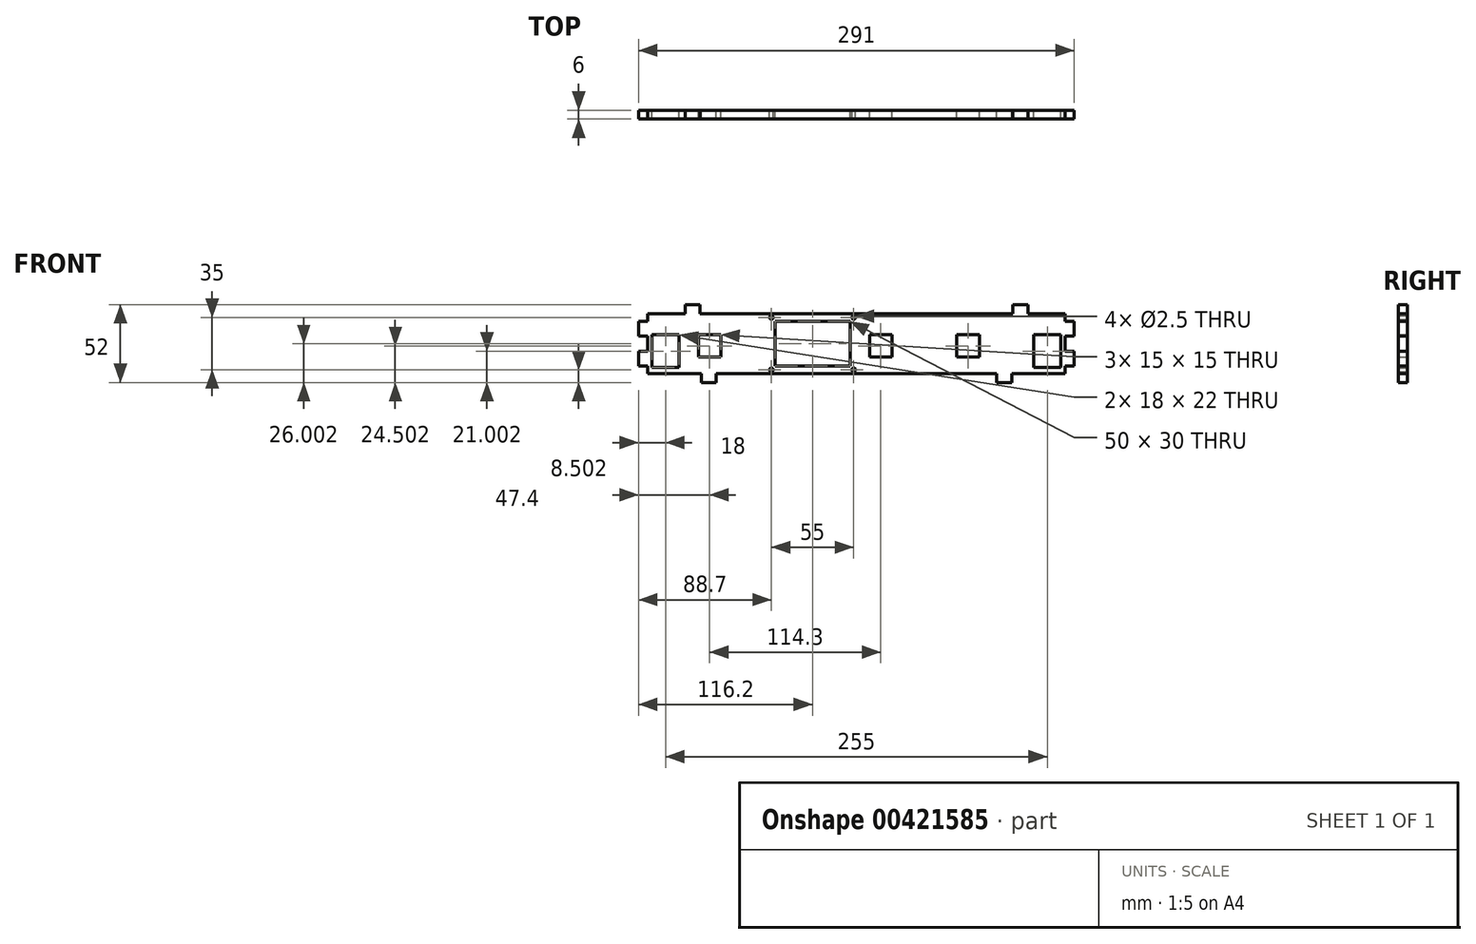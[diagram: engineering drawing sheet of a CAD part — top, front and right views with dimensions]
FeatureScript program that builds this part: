
annotation { "Feature Type Name" : "Feature", "Feature Type Description" : "" }
export const myFeature = defineFeature(function(context is Context, id is Id, definition is map)
    precondition{}
    {
        {
            var Q0;
            Q0=qCreatedBy(makeId("Front.planeOp"),FACE);
            var sketch = newSketch(context, id + "F0", { "sketchPlane" : qUnion([Q0])});
            skLineSegment(sketch, "E0", {"start": v(-139.5, -18.73) * mm, "end": v(-103.67, -18.73) * mm});
            skLineSegment(sketch, "E1.MirrorCS", {"start": v(-139.5, 21.27) * mm, "end": v(-114.5, 21.27) * mm});
            skLineSegment(sketch, "E2.MirrorCS", {"start": v(-114.5, 27.27) * mm, "end": v(-104.5, 27.27) * mm});
            skLineSegment(sketch, "E3.MirrorCS", {"start": v(-139.5, 16.27) * mm, "end": v(-139.5, 21.27) * mm});
            skLineSegment(sketch, "E4.MirrorCS", {"start": v(-139.5, 6.27) * mm, "end": v(-145.5, 6.27) * mm});
            skLineSegment(sketch, "E5.MirrorCS", {"start": v(-139.5, -3.73) * mm, "end": v(-139.5, 6.27) * mm});
            skLineSegment(sketch, "E6.MirrorCS", {"start": v(-145.5, -3.73) * mm, "end": v(-139.5, -3.73) * mm});
            skLineSegment(sketch, "E7", {"start": v(-103.67, -24.73) * mm, "end": v(-103.67, -18.73) * mm});
            skLineSegment(sketch, "E8", {"start": v(-114.5, 21.27) * mm, "end": v(-114.5, 27.27) * mm});
            skLineSegment(sketch, "E9", {"start": v(-139.5, -18.73) * mm, "end": v(-139.5, -13.73) * mm});
            skLineSegment(sketch, "E10", {"start": v(-93.67, -18.73) * mm, "end": v(0, -18.73) * mm});
            skLineSegment(sketch, "E11", {"start": v(-104.5, 27.27) * mm, "end": v(-104.5, 21.27) * mm});
            skLineSegment(sketch, "E12.MirrorCS", {"start": v(93.67, -24.73) * mm, "end": v(93.67, -18.73) * mm});
            skLineSegment(sketch, "E13.MirrorCS", {"start": v(104.5, 27.27) * mm, "end": v(104.5, 21.27) * mm});
            skLineSegment(sketch, "E14.MirrorCS", {"start": v(114.5, 21.27) * mm, "end": v(114.5, 27.27) * mm});
            skLineSegment(sketch, "E15.MirrorCS", {"start": v(103.67, -24.73) * mm, "end": v(103.67, -18.73) * mm});
            skLineSegment(sketch, "E16.MirrorCS", {"start": v(103.67, -24.73) * mm, "end": v(93.67, -24.73) * mm});
            skLineSegment(sketch, "E17.MirrorCS", {"start": v(139.5, -18.73) * mm, "end": v(103.67, -18.73) * mm});
            skLineSegment(sketch, "E18.MirrorCS", {"start": v(114.5, 27.27) * mm, "end": v(104.5, 27.27) * mm});
            skLineSegment(sketch, "E19.MirrorCS", {"start": v(139.5, 21.27) * mm, "end": v(114.5, 21.27) * mm});
            skLineSegment(sketch, "E20.MirrorCS", {"start": v(93.67, -18.73) * mm, "end": v(0, -18.73) * mm});
            skLineSegment(sketch, "E21.bottom", {"start": v(-136.5, 7.27) * mm, "end": v(-118.5, 7.27) * mm});
            skLineSegment(sketch, "E21.top", {"start": v(-136.5, -14.73) * mm, "end": v(-118.5, -14.73) * mm});
            skLineSegment(sketch, "E21.left", {"start": v(-136.5, 7.27) * mm, "end": v(-136.5, -14.73) * mm});
            skLineSegment(sketch, "E21.right", {"start": v(-118.5, 7.27) * mm, "end": v(-118.5, -14.73) * mm});
            skLineSegment(sketch, "E22.MirrorCS", {"start": v(118.5, 7.27) * mm, "end": v(118.5, -14.73) * mm});
            skLineSegment(sketch, "E23.MirrorCS", {"start": v(136.5, 7.27) * mm, "end": v(118.5, 7.27) * mm});
            skLineSegment(sketch, "E24.MirrorCS", {"start": v(136.5, 7.27) * mm, "end": v(136.5, -14.73) * mm});
            skLineSegment(sketch, "E25.MirrorCS", {"start": v(136.5, -14.73) * mm, "end": v(118.5, -14.73) * mm});
            skLineSegment(sketch, "E26.MirrorCS", {"start": v(67.1, -7.73) * mm, "end": v(67.1, 7.27) * mm});
            skLineSegment(sketch, "E27.bottom", {"start": v(8.7, -7.73) * mm, "end": v(23.7, -7.73) * mm});
            skLineSegment(sketch, "E27.top", {"start": v(8.7, 7.27) * mm, "end": v(23.7, 7.27) * mm});
            skLineSegment(sketch, "E27.left", {"start": v(8.7, -7.73) * mm, "end": v(8.7, 7.27) * mm});
            skLineSegment(sketch, "E27.right", {"start": v(23.7, -7.73) * mm, "end": v(23.7, 7.27) * mm});
            skLineSegment(sketch, "E28.bottom", {"start": v(-90.6, 7.27) * mm, "end": v(-105.6, 7.27) * mm});
            skLineSegment(sketch, "E28.top", {"start": v(-90.6, -7.73) * mm, "end": v(-105.6, -7.73) * mm});
            skLineSegment(sketch, "E28.left", {"start": v(-90.6, 7.27) * mm, "end": v(-90.6, -7.73) * mm});
            skLineSegment(sketch, "E28.right", {"start": v(-105.6, 7.27) * mm, "end": v(-105.6, -7.73) * mm});
            skLineSegment(sketch, "E29", {"start": v(67.1, 7.27) * mm, "end": v(82.1, 7.27) * mm});
            skLineSegment(sketch, "E30", {"start": v(82.1, 7.27) * mm, "end": v(82.1, -7.73) * mm});
            skLineSegment(sketch, "E31", {"start": v(67.1, -7.73) * mm, "end": v(82.1, -7.73) * mm});
            skLineSegment(sketch, "E32.bottom", {"start": v(-54.3, 16.27) * mm, "end": v(-4.3, 16.27) * mm});
            skLineSegment(sketch, "E32.top", {"start": v(-54.3, -13.73) * mm, "end": v(-4.3, -13.73) * mm});
            skLineSegment(sketch, "E32.left", {"start": v(-54.3, 16.27) * mm, "end": v(-54.3, -13.73) * mm});
            skLineSegment(sketch, "E32.right", {"start": v(-4.3, 16.27) * mm, "end": v(-4.3, -13.73) * mm});
            skCircle(sketch, "E33", {"center": v(-56.8, 18.77) * mm, "radius": 1.25 * mm});
            skPoint(sketch, "E34.endSnap0", {"position": v(-54.3, 1.27) * mm});
            skCircle(sketch, "E35.MirrorC", {"center": v(-1.8, 18.77) * mm, "radius": 1.25 * mm});
            skCircle(sketch, "E36.MirrorC", {"center": v(-56.8, -16.23) * mm, "radius": 1.25 * mm});
            skCircle(sketch, "E37.MirrorC", {"center": v(-1.8, -16.23) * mm, "radius": 1.25 * mm});
            skLineSegment(sketch, "E38", {"start": v(-103.67, -24.73) * mm, "end": v(-93.67, -24.73) * mm});
            skLineSegment(sketch, "E39", {"start": v(-93.67, -24.73) * mm, "end": v(-93.67, -18.73) * mm});
            skLineSegment(sketch, "E40", {"start": v(-145.5, -3.73) * mm, "end": v(-145.5, -13.73) * mm});
            skLineSegment(sketch, "E41", {"start": v(-145.5, -13.73) * mm, "end": v(-139.5, -13.73) * mm});
            skLineSegment(sketch, "E42", {"start": v(-145.5, 6.27) * mm, "end": v(-145.5, 16.27) * mm});
            skLineSegment(sketch, "E43", {"start": v(-145.5, 16.27) * mm, "end": v(-139.5, 16.27) * mm});
            skLineSegment(sketch, "E44.MirrorCS", {"start": v(145.5, -13.73) * mm, "end": v(139.5, -13.73) * mm});
            skLineSegment(sketch, "E45.MirrorCS", {"start": v(139.5, 6.27) * mm, "end": v(145.5, 6.27) * mm});
            skLineSegment(sketch, "E46.MirrorCS", {"start": v(139.5, -18.73) * mm, "end": v(139.5, -13.73) * mm});
            skLineSegment(sketch, "E47.MirrorCS", {"start": v(145.5, 6.27) * mm, "end": v(145.5, 16.27) * mm});
            skLineSegment(sketch, "E48.MirrorCS", {"start": v(139.5, 16.27) * mm, "end": v(139.5, 21.27) * mm});
            skLineSegment(sketch, "E49.MirrorCS", {"start": v(145.5, 16.27) * mm, "end": v(139.5, 16.27) * mm});
            skLineSegment(sketch, "E50.MirrorCS", {"start": v(139.5, -3.73) * mm, "end": v(139.5, 6.27) * mm});
            skLineSegment(sketch, "E51.MirrorCS", {"start": v(145.5, -3.73) * mm, "end": v(145.5, -13.73) * mm});
            skLineSegment(sketch, "E52.MirrorCS", {"start": v(145.5, -3.73) * mm, "end": v(139.5, -3.73) * mm});
            skLineSegment(sketch, "E53", {"start": v(-104.5, 21.27) * mm, "end": v(0, 21.27) * mm});
            skLineSegment(sketch, "E54.MirrorCS", {"start": v(104.5, 21.27) * mm, "end": v(0, 21.27) * mm});
            skSolve(sketch);
        }
        {
            var Q0;
            Q0=makeQuery(id+"F0.imprint","IMPRINT",FACE,{"disambiguationData":[TD([[makeQuery(id+"F0.imprint","IMPRINT",EDGE,{"derivedFrom":sQuery(id+"F0.wireOp",EDGE,"E0")}),1.0]])]});
            extrude(context, id + "F1", {"entities" : qUnion([Q0]), "depth" : 6 * mm, "offsetDistance" : 25 * mm});
        }
    });
